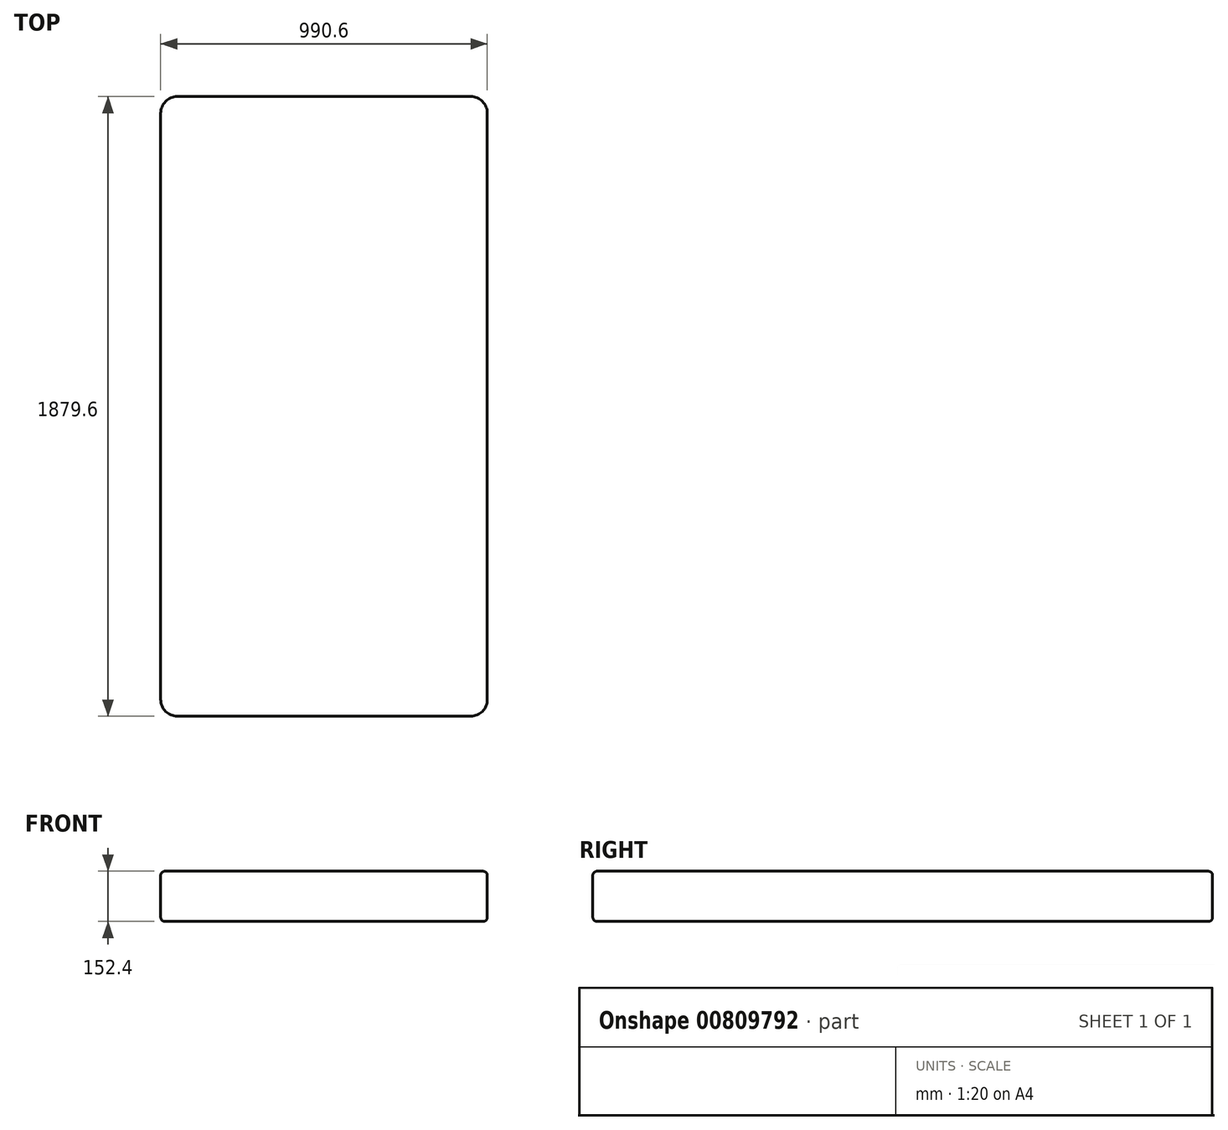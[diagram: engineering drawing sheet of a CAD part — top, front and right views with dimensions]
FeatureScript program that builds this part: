
annotation { "Feature Type Name" : "Feature", "Feature Type Description" : "" }
export const myFeature = defineFeature(function(context is Context, id is Id, definition is map)
    precondition{}
    {
        {
            var Q0;
            Q0=qCreatedBy(makeId("Top.planeOp"),FACE);
            var sketch = newSketch(context, id + "F0", { "sketchPlane" : qUnion([Q0])});
            skLineSegment(sketch, "E0.bottom", {"start": v(-495.3, 939.8) * mm, "end": v(495.3, 939.8) * mm});
            skLineSegment(sketch, "E0.top", {"start": v(-495.3, -939.8) * mm, "end": v(495.3, -939.8) * mm});
            skLineSegment(sketch, "E0.left", {"start": v(-495.3, 939.8) * mm, "end": v(-495.3, -939.8) * mm});
            skLineSegment(sketch, "E0.right", {"start": v(495.3, 939.8) * mm, "end": v(495.3, -939.8) * mm});
            skLineSegment(sketch, "E1", {"start": v(-495.3, 939.8) * mm, "end": v(495.3, -939.8) * mm, "construction": true});
            skSolve(sketch);
        }
        {
            var Q0;
            Q0 = qSketchRegion(id + "F0", true);
            extrude(context, id + "F1", {"entities" : qUnion([Q0]), "depth" : 152.4 * mm, "offsetDistance" : 25.4 * mm});
        }
        {
            var Q0;
            Q0=makeQuery(id+"F1.opExtrude","CAP_EDGE",EDGE,{"disambiguationData":[OSD([sQuery(id+"F0.wireOp",EDGE,"E0.left")])],"isStart":false});
            var Q1;
            Q1=makeQuery(id+"F1.opExtrude","CAP_EDGE",EDGE,{"disambiguationData":[OSD([sQuery(id+"F0.wireOp",EDGE,"E0.top")])],"isStart":false});
            var Q2;
            Q2=makeQuery(id+"F1.opExtrude","CAP_EDGE",EDGE,{"disambiguationData":[OSD([sQuery(id+"F0.wireOp",EDGE,"E0.right")])],"isStart":false});
            var Q3;
            Q3=makeQuery(id+"F1.opExtrude","CAP_EDGE",EDGE,{"disambiguationData":[OSD([sQuery(id+"F0.wireOp",EDGE,"E0.bottom")])],"isStart":false});
            var Q4;
            Q4=makeQuery(id+"F1.opExtrude","CAP_EDGE",EDGE,{"disambiguationData":[OSD([sQuery(id+"F0.wireOp",EDGE,"E0.right")])],"isStart":true});
            var Q5;
            Q5=makeQuery(id+"F1.opExtrude","CAP_EDGE",EDGE,{"disambiguationData":[OSD([sQuery(id+"F0.wireOp",EDGE,"E0.top")])],"isStart":true});
            var Q6;
            Q6=makeQuery(id+"F1.opExtrude","CAP_EDGE",EDGE,{"disambiguationData":[OSD([sQuery(id+"F0.wireOp",EDGE,"E0.left")])],"isStart":true});
            var Q7;
            Q7=makeQuery(id+"F1.opExtrude","CAP_EDGE",EDGE,{"disambiguationData":[OSD([sQuery(id+"F0.wireOp",EDGE,"E0.bottom")])],"isStart":true});
            fillet(context, id + "F2", {"entities" : qUnion([Q0, Q1, Q2, Q3, Q4, Q5, Q6, Q7]), "radius" : 12.7 * mm, "tangentPropagation" : true, "allowEdgeOverflow" : false});
        }
        {
            var Q0;
            Q0=makeQuery(id+"F1.opExtrude","SWEPT_EDGE",EDGE,{"disambiguationData":[OSD([sQuery(id+"F0.wireOp",EDGE,"E0.top"),sQuery(id+"F0.wireOp",EDGE,"E0.left")])]});
            var Q1;
            Q1=makeQuery(id+"F1.opExtrude","SWEPT_EDGE",EDGE,{"disambiguationData":[OSD([sQuery(id+"F0.wireOp",EDGE,"E0.top"),sQuery(id+"F0.wireOp",EDGE,"E0.right")])]});
            var Q2;
            Q2=makeQuery(id+"F1.opExtrude","SWEPT_EDGE",EDGE,{"disambiguationData":[OSD([sQuery(id+"F0.wireOp",EDGE,"E0.bottom"),sQuery(id+"F0.wireOp",EDGE,"E0.right")])]});
            var Q3;
            Q3=makeQuery(id+"F1.opExtrude","SWEPT_EDGE",EDGE,{"disambiguationData":[OSD([sQuery(id+"F0.wireOp",EDGE,"E0.bottom"),sQuery(id+"F0.wireOp",EDGE,"E0.left")])]});
            fillet(context, id + "F3", {"entities" : qUnion([Q0, Q1, Q2, Q3]), "radius" : 50.8 * mm, "tangentPropagation" : true, "allowEdgeOverflow" : false});
        }
    });
